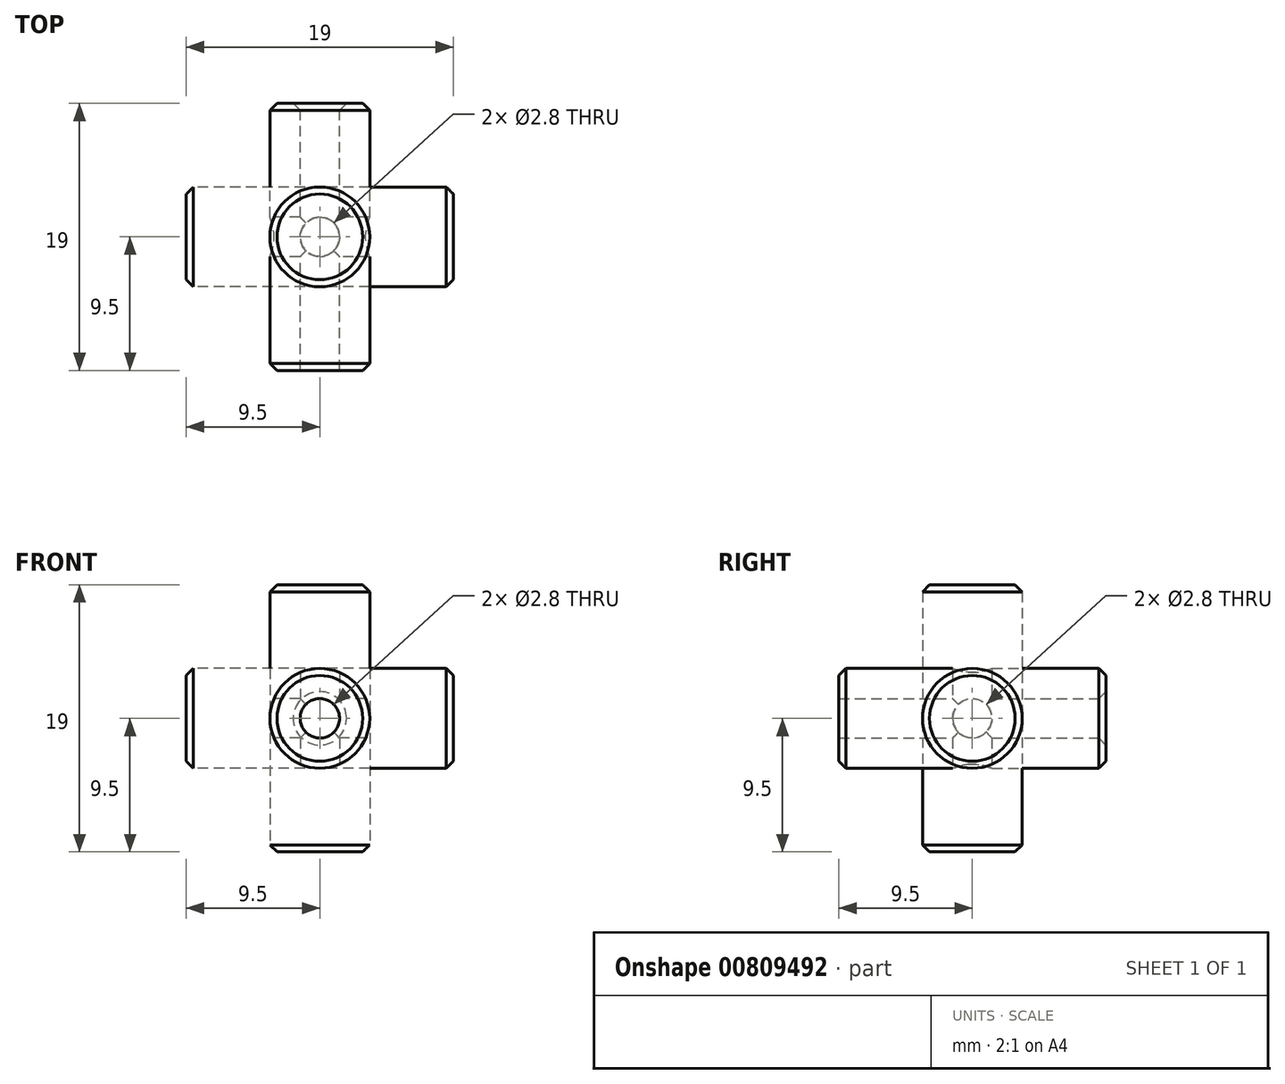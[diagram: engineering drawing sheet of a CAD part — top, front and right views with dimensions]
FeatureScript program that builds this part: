
annotation { "Feature Type Name" : "Feature", "Feature Type Description" : "" }
export const myFeature = defineFeature(function(context is Context, id is Id, definition is map)
    precondition{}
    {
        {
            var Q0;
            Q0=qCreatedBy(makeId("Front.planeOp"),FACE);
            var sketch = newSketch(context, id + "F0", { "sketchPlane" : qUnion([Q0])});
            skCircle(sketch, "E0", {"center": v(0, 0) * mm, "radius": 3.55 * mm});
            skSolve(sketch);
        }
        {
            var Q0;
            Q0 = qSketchRegion(id + "F0", true);
            extrude(context, id + "F1", {"entities" : qUnion([Q0]), "endBound" : BoundingType.SYMMETRIC, "depth" : 19 * mm, "offsetDistance" : 25 * mm});
        }
        {
            var Q0;
            Q0=qCreatedBy(makeId("Front.planeOp"),FACE);
            var sketch = newSketch(context, id + "F2", { "sketchPlane" : qUnion([Q0])});
            skCircle(sketch, "E1", {"center": v(0, 0) * mm, "radius": 1.4 * mm});
            skSolve(sketch);
        }
        {
            var Q0;
            Q0 = qSketchRegion(id + "F2", true);
            extrude(context, id + "F3", {"entities" : qUnion([Q0]), "endBound" : BoundingType.SYMMETRIC, "depth" : 20 * mm, "offsetDistance" : 25 * mm});
        }
        {
            var Q0;
            Q0=qCreatedBy(makeId("Front.planeOp"),FACE);
            var sketch = newSketch(context, id + "F4", { "sketchPlane" : qUnion([Q0])});
            skLineSegment(sketch, "E2.bottom", {"start": v(0, 0) * mm, "end": v(10, 0) * mm});
            skLineSegment(sketch, "E2.top", {"start": v(0, 10) * mm, "end": v(10, 10) * mm});
            skLineSegment(sketch, "E2.left", {"start": v(0, 0) * mm, "end": v(0, 10) * mm});
            skLineSegment(sketch, "E2.right", {"start": v(10, 0) * mm, "end": v(10, 10) * mm});
            skSolve(sketch);
        }
        {
            var Q0;
            Q0=makeQuery(id+"F4.imprint","IMPRINT",FACE,{"disambiguationData":[TD([[makeQuery(id+"F4.imprint","IMPRINT",EDGE,{"derivedFrom":sQuery(id+"F4.wireOp",EDGE,"E2.bottom")}),1.0]])]});
            extrude(context, id + "F5", {"entities" : qUnion([Q0]), "depth" : 10 * mm, "offsetDistance" : 25 * mm});
        }
        {
            var Q0;
            Q0=sQuery(id+"F0.wireOp",VERTEX,"E0.center");
            var Q1;
            Q1=makeQuery(id+"F5.opExtrude","CAP_VERTEX",VERTEX,{"disambiguationData":[OSD([sQuery(id+"F4.wireOp",EDGE,"E2.top"),sQuery(id+"F4.wireOp",EDGE,"E2.right")])],"isStart":false});
            var Q2;
            Q2=makeQuery(id+"F5.opExtrude","CAP_VERTEX",VERTEX,{"disambiguationData":[OSD([sQuery(id+"F4.wireOp",EDGE,"E2.bottom"),sQuery(id+"F4.wireOp",EDGE,"E2.right")])],"isStart":false});
            cPlane(context, id + "F6", {"entities" : qUnion([Q0, Q1, Q2]), "cplaneType" : CPlaneType.THREE_POINT, "offset" : 25 * mm, "width" : 150 * mm, "height" : 150 * mm});
        }
        {
            var Q0;
            Q0=qCreatedBy(id+"F6.planeOp",FACE);
            var sketch = newSketch(context, id + "F7", { "sketchPlane" : qUnion([Q0])});
            skLineSegment(sketch, "E3", {"start": v(0, 0) * mm, "end": v(14.14, 10) * mm});
            skSolve(sketch);
        }
        {
            var Q0;
            Q0=makeQuery(id+"F5.opExtrude","SWEPT_BODY",BODY,{"disambiguationData":[OSD([sQuery(id+"F4.wireOp",EDGE,"E2.bottom"),sQuery(id+"F4.wireOp",EDGE,"E2.top"),sQuery(id+"F4.wireOp",EDGE,"E2.left"),sQuery(id+"F4.wireOp",EDGE,"E2.right")])]});
            deleteBodies(context, id + "F8", {"entities" : qUnion([Q0])});
        }
        {
            var Q0;
            Q0=makeQuery(id+"F3.opExtrude","SWEPT_BODY",BODY,{"disambiguationData":[OSD([sQuery(id+"F2.wireOp",EDGE,"E1")])]});
            var Q1;
            Q1=makeQuery(id+"F1.opExtrude","SWEPT_BODY",BODY,{"disambiguationData":[OSD([sQuery(id+"F0.wireOp",EDGE,"E0")])]});
            var Q2;
            Q2=sQuery(id+"F7.wireOp",EDGE,"E3");
            circularPattern(context, id + "F9", {"entities" : qUnion([Q0, Q1]), "axis" : qUnion([Q2]), "angle" : 360 * degree, "instanceCount" : 3, "equalSpace" : true});
        }
        {
            var Q0;
            Q0=makeQuery(id+"F9.opPattern","COPY",BODY,{"derivedFrom":makeQuery(id+"F3.opExtrude","SWEPT_BODY",BODY,{"disambiguationData":[OSD([sQuery(id+"F2.wireOp",EDGE,"E1")])]}),"instanceName":"1"});
            var Q1;
            Q1=makeQuery(id+"F3.opExtrude","SWEPT_BODY",BODY,{"disambiguationData":[OSD([sQuery(id+"F2.wireOp",EDGE,"E1")])]});
            var Q2;
            Q2=makeQuery(id+"F9.opPattern","COPY",BODY,{"derivedFrom":makeQuery(id+"F3.opExtrude","SWEPT_BODY",BODY,{"disambiguationData":[OSD([sQuery(id+"F2.wireOp",EDGE,"E1")])]}),"instanceName":"2"});
            var Q3;
            Q3=makeQuery(id+"F1.opExtrude","SWEPT_BODY",BODY,{"disambiguationData":[OSD([sQuery(id+"F0.wireOp",EDGE,"E0")])]});
            booleanBodies(context, id + "F10", {"operationType" : BooleanOperationType.SUBTRACTION, "tools" : qUnion([Q0, Q1, Q2]), "targets" : qUnion([Q3])});
        }
        {
            var Q0;
            Q0=makeQuery(id+"F9.opPattern","COPY",FACE,{"derivedFrom":makeQuery(id+"F1.opExtrude","CAP_FACE",FACE,{"disambiguationData":[OSD([sQuery(id+"F0.wireOp",EDGE,"E0")])],"isStart":true}),"instanceName":"2"});
            var Q1;
            Q1=makeQuery(id+"F9.opPattern","COPY",EDGE,{"derivedFrom":makeQuery(id+"F1.opExtrude","CAP_EDGE",EDGE,{"disambiguationData":[OSD([sQuery(id+"F0.wireOp",EDGE,"E0")])],"isStart":false}),"instanceName":"1"});
            var Q2;
            Q2=makeQuery(id+"F9.opPattern","COPY",EDGE,{"derivedFrom":makeQuery(id+"F1.opExtrude","CAP_EDGE",EDGE,{"disambiguationData":[OSD([sQuery(id+"F0.wireOp",EDGE,"E0")])],"isStart":true}),"instanceName":"1"});
            var Q3;
            Q3=makeQuery(id+"F1.opExtrude","CAP_FACE",FACE,{"disambiguationData":[OSD([sQuery(id+"F0.wireOp",EDGE,"E0")])],"isStart":true});
            var Q4;
            Q4=makeQuery(id+"F9.opPattern","COPY",FACE,{"derivedFrom":makeQuery(id+"F1.opExtrude","CAP_FACE",FACE,{"disambiguationData":[OSD([sQuery(id+"F0.wireOp",EDGE,"E0")])],"isStart":false}),"instanceName":"2"});
            var Q5;
            Q5=makeQuery(id+"F1.opExtrude","CAP_EDGE",EDGE,{"disambiguationData":[OSD([sQuery(id+"F0.wireOp",EDGE,"E0")])],"isStart":false});
            chamfer(context, id + "F11", {"entities" : qUnion([Q0, Q1, Q2, Q3, Q4, Q5]), "width" : 0.5 * mm, "tangentPropagation" : true});
        }
    });
